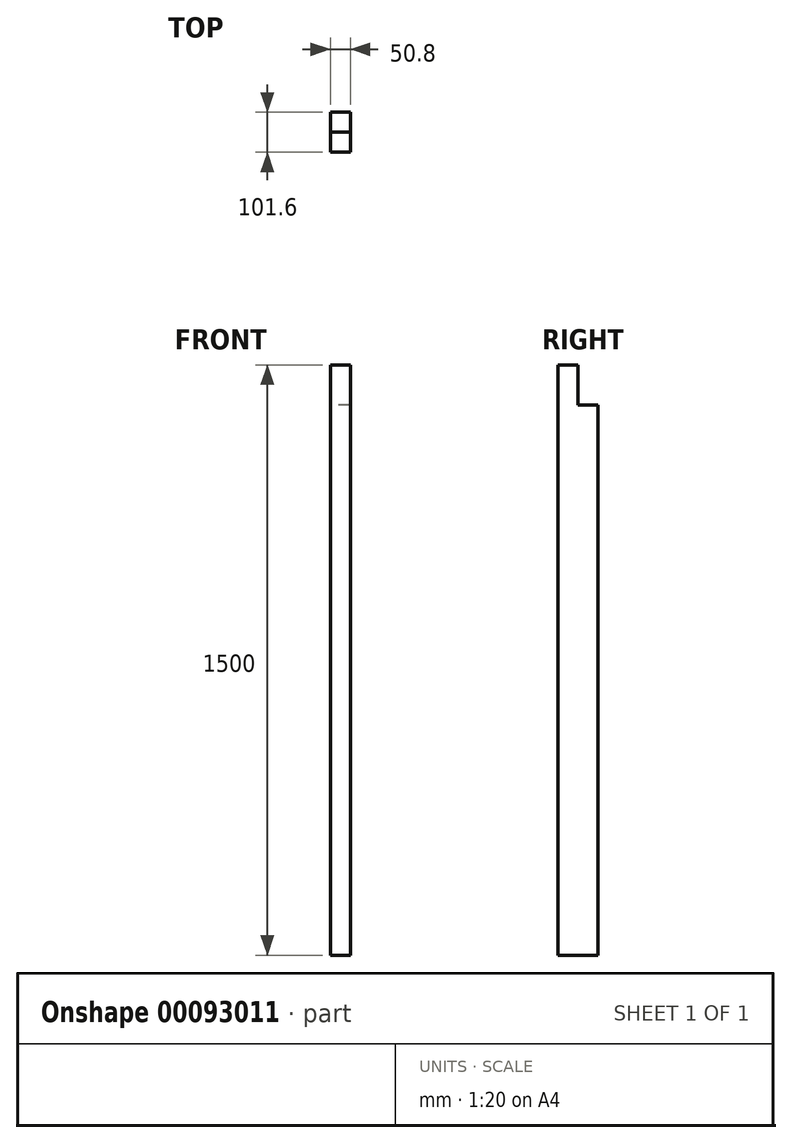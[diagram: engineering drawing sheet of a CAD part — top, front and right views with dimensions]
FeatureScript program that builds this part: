
annotation { "Feature Type Name" : "Feature", "Feature Type Description" : "" }
export const myFeature = defineFeature(function(context is Context, id is Id, definition is map)
    precondition{}
    {
        {
            var Q0;
            Q0=qCreatedBy(makeId("Top.planeOp"),FACE);
            var sketch = newSketch(context, id + "F0", { "sketchPlane" : qUnion([Q0])});
            skLineSegment(sketch, "E0.bottom", {"start": v(25.4, 50.8) * mm, "end": v(-25.4, 50.8) * mm});
            skLineSegment(sketch, "E0.top", {"start": v(25.4, -50.8) * mm, "end": v(-25.4, -50.8) * mm});
            skLineSegment(sketch, "E0.left", {"start": v(25.4, 50.8) * mm, "end": v(25.4, -50.8) * mm});
            skLineSegment(sketch, "E0.right", {"start": v(-25.4, 50.8) * mm, "end": v(-25.4, -50.8) * mm});
            skPoint(sketch, "E0.middle", {"position": v(0, 0) * mm});
            skSolve(sketch);
        }
        {
            var Q0;
            Q0=makeQuery(id+"F0.imprint","IMPRINT",FACE,{"disambiguationData":[TD([[makeQuery(id+"F0.imprint","IMPRINT",EDGE,{"derivedFrom":sQuery(id+"F0.wireOp",EDGE,"E0.bottom")}),1.0]])]});
            extrude(context, id + "F1", {"entities" : qUnion([Q0]), "depth" : 1500 * mm});
        }
        {
            var Q0;
            Q0=qCreatedBy(makeId("Right.planeOp"),FACE);
            var sketch = newSketch(context, id + "F2", { "sketchPlane" : qUnion([Q0])});
            skLineSegment(sketch, "E1.0", {"start": v(50.8, 1500) * mm, "end": v(0, 1500) * mm});
            skLineSegment(sketch, "E2.0", {"start": v(50.8, 1500) * mm, "end": v(50.8, 1398.4) * mm});
            skLineSegment(sketch, "E3", {"start": v(0, 1500) * mm, "end": v(0, 1398.4) * mm});
            skLineSegment(sketch, "E4", {"start": v(0, 1398.4) * mm, "end": v(50.8, 1398.4) * mm});
            skSolve(sketch);
        }
        {
            var Q0;
            Q0 = qSketchRegion(id + "F2", true);
            extrude(context, id + "F3", {"entities" : qUnion([Q0]), "operationType" : NewBodyOperationType.REMOVE, "endBound" : BoundingType.SYMMETRIC, "depth" : 50.8 * mm});
        }
    });
